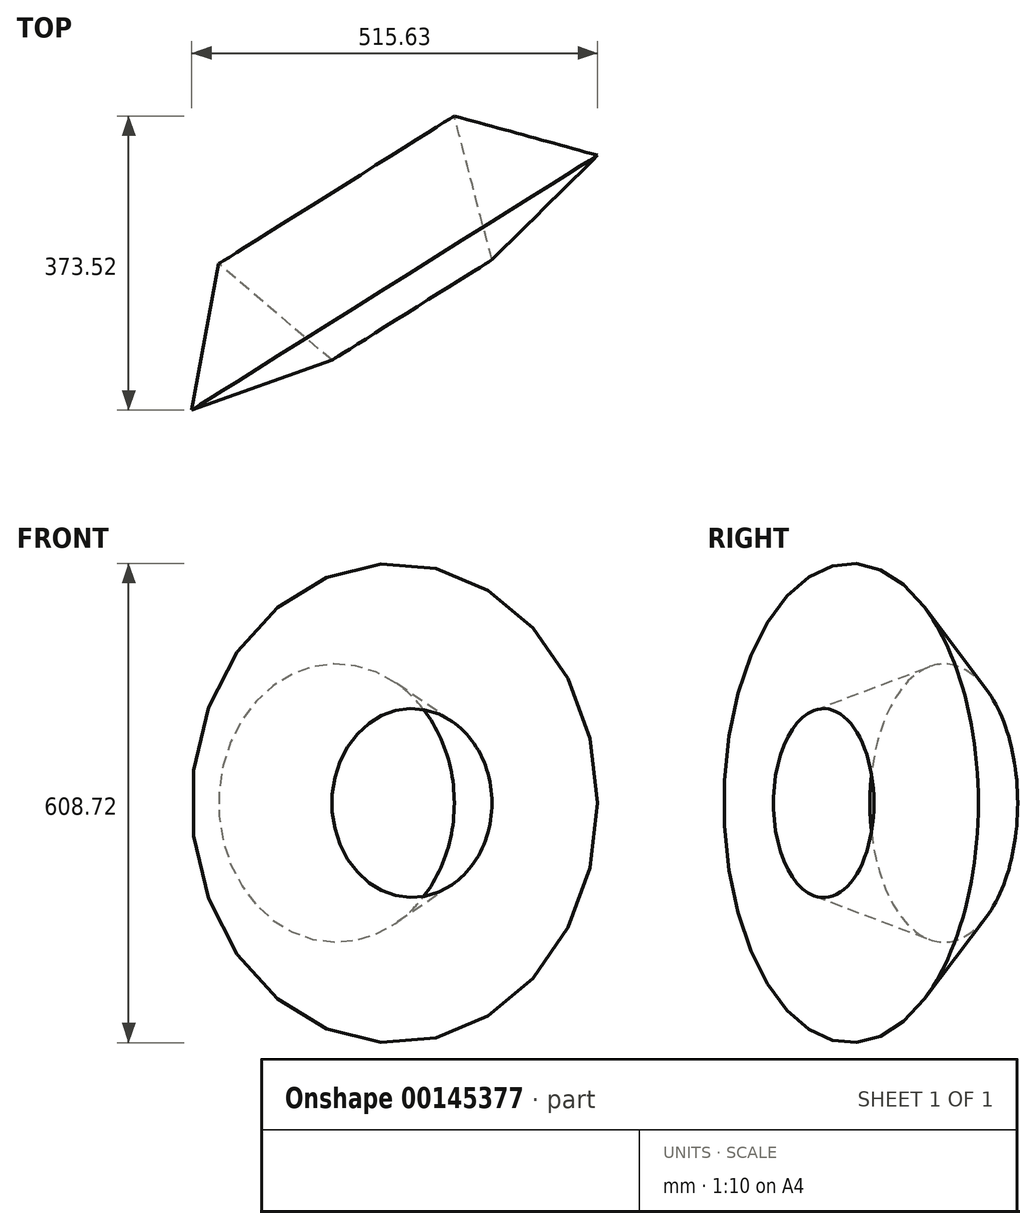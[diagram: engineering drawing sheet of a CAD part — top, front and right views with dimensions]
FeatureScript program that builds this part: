
annotation { "Feature Type Name" : "Feature", "Feature Type Description" : "" }
export const myFeature = defineFeature(function(context is Context, id is Id, definition is map)
    precondition{}
    {
        {
            var Q0;
            Q0=qCreatedBy(makeId("Top.planeOp"),FACE);
            var sketch = newSketch(context, id + "F0", { "sketchPlane" : qUnion([Q0])});
            skCircle(sketch, "E0.cCircle", {"center": v(-94.68, -26.97) * mm, "radius": 54.52 * mm, "construction": true});
            skLineSegment(sketch, "E0.0", {"start": v(12.56, -46.72) * mm, "end": v(-165.41, -109.96) * mm});
            skLineSegment(sketch, "E0.1", {"start": v(-165.41, -109.96) * mm, "end": v(-131.2, 75.78) * mm});
            skLineSegment(sketch, "E0.2", {"start": v(-131.2, 75.78) * mm, "end": v(12.56, -46.72) * mm});
            skPoint(sketch, "E0.0.midPoint", {"position": v(-76.43, -78.34) * mm});
            skLineSegment(sketch, "E1", {"start": v(-165.41, -109.96) * mm, "end": v(12.56, -46.72) * mm});
            skCircle(sketch, "E2", {"center": v(-94.68, -26.97) * mm, "radius": 46.66 * mm});
            skLineSegment(sketch, "E3", {"start": v(-165.41, -109.96) * mm, "end": v(-124.22, -225.88) * mm});
            skLineSegment(sketch, "E4", {"start": v(-124.22, -225.88) * mm, "end": v(53.75, -162.64) * mm});
            skLineSegment(sketch, "E5", {"start": v(53.75, -162.64) * mm, "end": v(12.56, -46.72) * mm});
            skLineSegment(sketch, "E6", {"start": v(62.8, -99.63) * mm, "end": v(175.95, -72.97) * mm});
            skLineSegment(sketch, "E7", {"start": v(147.05, -35.3) * mm, "end": v(74.4, 80.5) * mm});
            skSolve(sketch);
        }
        {
            var Q0;
            Q0=makeQuery(id+"F0.imprint","IMPRINT",FACE,{"disambiguationData":[TD([[makeQuery(id+"F0.imprint","IMPRINT",EDGE,{"derivedFrom":sQuery(id+"F0.wireOp",EDGE,"E1")}),-1.0]])]});
            var Q1;
            Q1=makeQuery(id+"F0.imprint","IMPRINT",FACE,{"disambiguationData":[TD([[makeQuery(id+"F0.imprint","IMPRINT",EDGE,{"derivedFrom":sQuery(id+"F0.wireOp",EDGE,"E0.1")}),-1.0]])]});
            var Q2;
            Q2=makeQuery(id+"F0.imprint","IMPRINT",FACE,{"disambiguationData":[TD([[makeQuery(id+"F0.imprint","IMPRINT",EDGE,{"derivedFrom":sQuery(id+"F0.wireOp",EDGE,"E2")}),1.0]])]});
            var Q3;
            Q3=sQuery(id+"F0.wireOp",EDGE,"E7");
            revolve(context, id + "F1", {"entities" : qUnion([Q0, Q1, Q2]), "axis" : qUnion([Q3]), "revolveType" : RevolveType.FULL});
        }
    });
